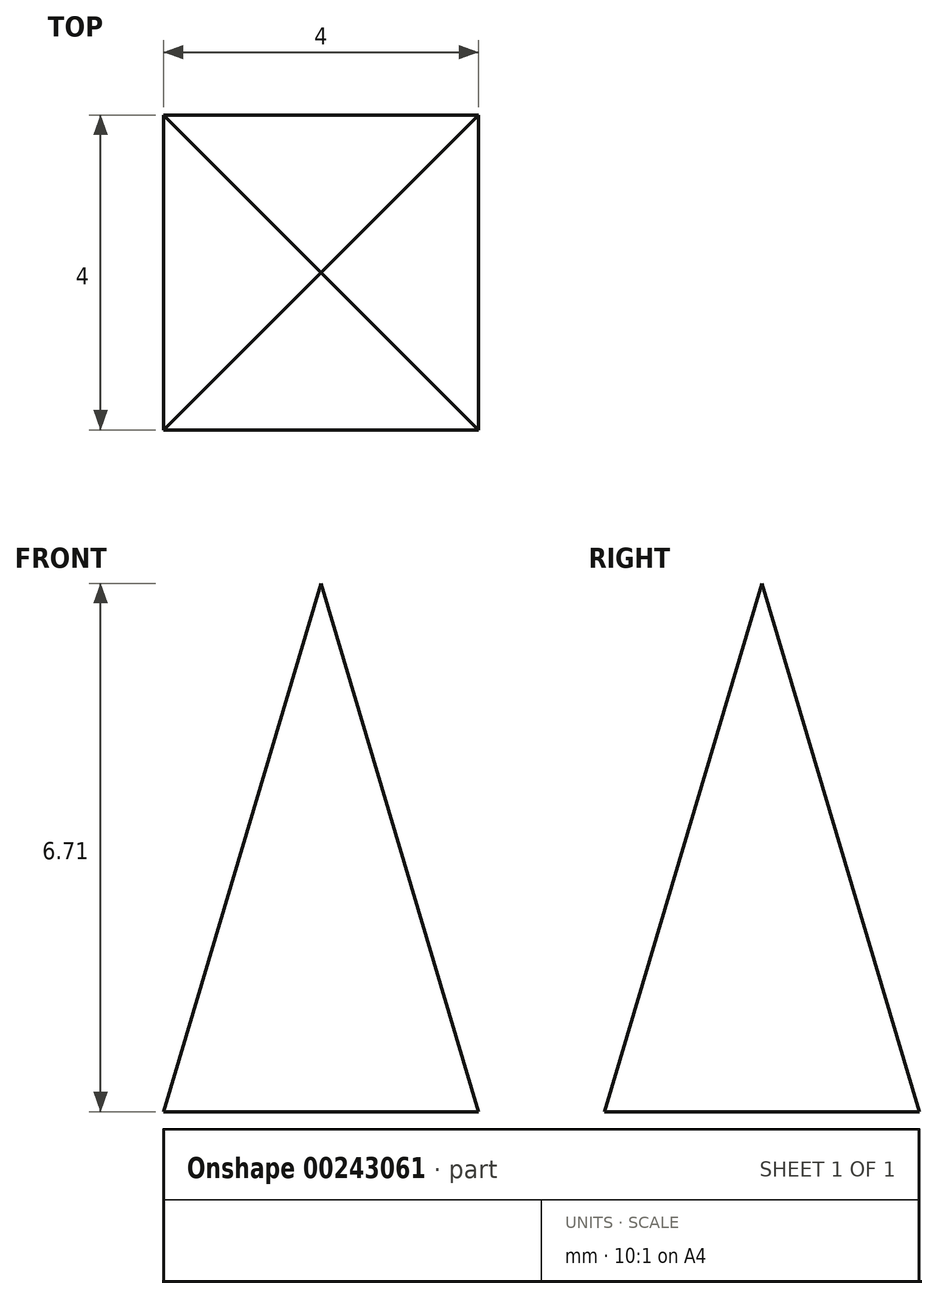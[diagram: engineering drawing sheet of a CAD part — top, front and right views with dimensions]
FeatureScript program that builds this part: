
annotation { "Feature Type Name" : "Feature", "Feature Type Description" : "" }
export const myFeature = defineFeature(function(context is Context, id is Id, definition is map)
    precondition{}
    {
        {
            var Q0;
            Q0=qCreatedBy(makeId("Front.planeOp"),FACE);
            var sketch = newSketch(context, id + "F0", { "sketchPlane" : qUnion([Q0])});
            skLineSegment(sketch, "E0", {"start": v(0, 0) * mm, "end": v(4, 0) * mm});
            skLineSegment(sketch, "E1", {"start": v(0, 0) * mm, "end": v(2, 0) * mm, "construction": true});
            skLineSegment(sketch, "E2", {"start": v(2, 6.7) * mm, "end": v(4, 0) * mm});
            skLineSegment(sketch, "E3", {"start": v(2, 6.7) * mm, "end": v(0, 0) * mm});
            skSolve(sketch);
        }
        {
            var Q0;
            Q0=makeQuery(id+"F0.imprint","IMPRINT",FACE,{"disambiguationData":[TD([[makeQuery(id+"F0.imprint","IMPRINT",EDGE,{"derivedFrom":sQuery(id+"F0.wireOp",EDGE,"E0")}),1.0]])]});
            extrude(context, id + "F1", {"entities" : qUnion([Q0]), "oppositeDirection" : true, "depth" : 4 * mm});
        }
        {
            var Q0;
            Q0=makeQuery(id+"F1.opExtrude","SWEPT_EDGE",EDGE,{"disambiguationData":[OSD([sQuery(id+"F0.wireOp",EDGE,"E2"),sQuery(id+"F0.wireOp",EDGE,"E3")])]});
            cPoint(context, id + "F2", {"entities" : qUnion([Q0]), "parameter" : 0.5});
        }
        {
            var Q0;
            Q0 = qCreatedBy(id + "F2" ,VERTEX);
            var Q1;
            Q1=makeQuery(id+"F1.opExtrude","CAP_VERTEX",VERTEX,{"disambiguationData":[OSD([sQuery(id+"F0.wireOp",EDGE,"E0"),sQuery(id+"F0.wireOp",EDGE,"E2")])],"isStart":true});
            var Q2;
            Q2=qCreatedBy(makeId("Origin.pointOp"),VERTEX);
            cPlane(context, id + "F3", {"entities" : qUnion([Q0, Q1, Q2]), "cplaneType" : CPlaneType.THREE_POINT, "offset" : 25 * mm, "width" : 150 * mm, "height" : 150 * mm});
        }
        {
            var Q0;
            Q0=qCreatedBy(id+"F3.planeOp",FACE);
            var sketch = newSketch(context, id + "F4", { "sketchPlane" : qUnion([Q0])});
            skPoint(sketch, "E4.0", {"position": v(2, 7) * mm});
            skPoint(sketch, "E5.0", {"position": v(4, 0) * mm});
            skPoint(sketch, "E6.0", {"position": v(0, 0) * mm});
            skLineSegment(sketch, "E7", {"start": v(2, 7) * mm, "end": v(4, 0) * mm});
            skLineSegment(sketch, "E8", {"start": v(0, 0) * mm, "end": v(2, 7) * mm});
            skLineSegment(sketch, "E9", {"start": v(0, 0) * mm, "end": v(4, 0) * mm});
            skSolve(sketch);
        }
        {
            var Q0;
            Q0 = qSketchRegion(id + "F4", true);
            extrude(context, id + "F5", {"entities" : qUnion([Q0]), "operationType" : NewBodyOperationType.REMOVE, "depth" : 25 * mm});
        }
        {
            var Q0;
            Q0=makeQuery(id+"F5.boolean.opBoolean","COPY",VERTEX,{"derivedFrom":makeQuery(id+"F5.opExtrude","CAP_VERTEX",VERTEX,{"disambiguationData":[OSD([sQuery(id+"F4.wireOp",EDGE,"E7"),sQuery(id+"F4.wireOp",EDGE,"E8")])],"isStart":true})});
            var Q1;
            Q1=makeQuery(id+"F1.opExtrude","CAP_VERTEX",VERTEX,{"disambiguationData":[OSD([sQuery(id+"F0.wireOp",EDGE,"E0"),sQuery(id+"F0.wireOp",EDGE,"E2")])],"isStart":false});
            var Q2;
            Q2=makeQuery(id+"F1.opExtrude","CAP_VERTEX",VERTEX,{"disambiguationData":[OSD([sQuery(id+"F0.wireOp",EDGE,"E0"),sQuery(id+"F0.wireOp",EDGE,"E3")])],"isStart":false});
            cPlane(context, id + "F6", {"entities" : qUnion([Q0, Q1, Q2]), "cplaneType" : CPlaneType.THREE_POINT, "offset" : 25 * mm, "width" : 150 * mm, "height" : 150 * mm});
        }
        {
            var Q0;
            Q0=qCreatedBy(id+"F6.planeOp",FACE);
            var sketch = newSketch(context, id + "F7", { "sketchPlane" : qUnion([Q0])});
            skPoint(sketch, "E10.0", {"position": v(2, 5.86) * mm});
            skPoint(sketch, "E11.0", {"position": v(4, -1.14) * mm});
            skPoint(sketch, "E12.0", {"position": v(0, -1.14) * mm});
            skLineSegment(sketch, "E13", {"start": v(2, 5.86) * mm, "end": v(4, -1.14) * mm});
            skLineSegment(sketch, "E14", {"start": v(4, -1.14) * mm, "end": v(0, -1.14) * mm});
            skLineSegment(sketch, "E15", {"start": v(2, 5.86) * mm, "end": v(0, -1.14) * mm});
            skSolve(sketch);
        }
        {
            var Q0;
            Q0 = qSketchRegion(id + "F7", true);
            extrude(context, id + "F8", {"entities" : qUnion([Q0]), "operationType" : NewBodyOperationType.REMOVE, "oppositeDirection" : true, "depth" : 25 * mm});
        }
    });
